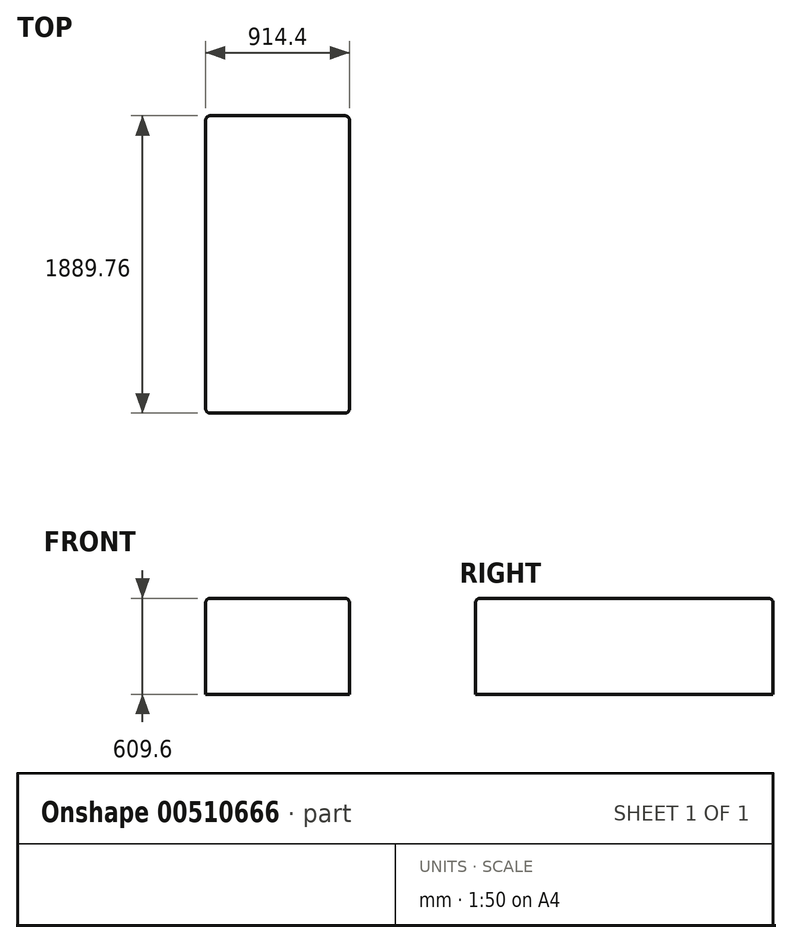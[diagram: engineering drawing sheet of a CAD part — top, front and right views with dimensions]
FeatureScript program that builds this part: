
annotation { "Feature Type Name" : "Feature", "Feature Type Description" : "" }
export const myFeature = defineFeature(function(context is Context, id is Id, definition is map)
    precondition{}
    {
        {
            var Q0;
            Q0=qCreatedBy(makeId("Top.planeOp"),FACE);
            var sketch = newSketch(context, id + "F0", { "sketchPlane" : qUnion([Q0])});
            skLineSegment(sketch, "E0.bottom", {"start": v(-470.27, 741.45) * mm, "end": v(444.13, 741.45) * mm});
            skLineSegment(sketch, "E0.top", {"start": v(-470.27, -1148.3) * mm, "end": v(444.13, -1148.3) * mm});
            skLineSegment(sketch, "E0.left", {"start": v(-470.27, 741.45) * mm, "end": v(-470.27, -1148.3) * mm});
            skLineSegment(sketch, "E0.right", {"start": v(444.13, 741.45) * mm, "end": v(444.13, -1148.3) * mm});
            skSolve(sketch);
        }
        {
            var Q0;
            Q0 = qSketchRegion(id + "F0", true);
            extrude(context, id + "F1", {"entities" : qUnion([Q0]), "depth" : 609.6 * mm, "offsetDistance" : 30.48 * mm});
        }
        {
            var Q0;
            Q0=makeQuery(id+"F1.opExtrude","CAP_EDGE",EDGE,{"disambiguationData":[OSD([sQuery(id+"F0.wireOp",EDGE,"E0.left")])],"isStart":false});
            var Q1;
            Q1=makeQuery(id+"F1.opExtrude","CAP_EDGE",EDGE,{"disambiguationData":[OSD([sQuery(id+"F0.wireOp",EDGE,"E0.bottom")])],"isStart":false});
            var Q2;
            Q2=makeQuery(id+"F1.opExtrude","CAP_EDGE",EDGE,{"disambiguationData":[OSD([sQuery(id+"F0.wireOp",EDGE,"E0.right")])],"isStart":false});
            var Q3;
            Q3=makeQuery(id+"F1.opExtrude","CAP_EDGE",EDGE,{"disambiguationData":[OSD([sQuery(id+"F0.wireOp",EDGE,"E0.top")])],"isStart":false});
            fillet(context, id + "F2", {"entities" : qUnion([Q0, Q1, Q2, Q3]), "radius" : 30.48 * mm, "tangentPropagation" : true, "allowEdgeOverflow" : false});
        }
        {
            var Q0;
            Q0=makeQuery(id+"F2.opFillet","BLEND_EDGE",EDGE,{"blendedFrom":[makeQuery(id+"F1.opExtrude","CAP_EDGE",EDGE,{"disambiguationData":[OSD([sQuery(id+"F0.wireOp",EDGE,"E0.bottom")])],"isStart":false}),makeQuery(id+"F1.opExtrude","CAP_EDGE",EDGE,{"disambiguationData":[OSD([sQuery(id+"F0.wireOp",EDGE,"E0.left")])],"isStart":false})],"blendedInto":[]});
            var Q1;
            Q1=makeQuery(id+"F2.opFillet","BLEND_EDGE",EDGE,{"blendedFrom":[makeQuery(id+"F1.opExtrude","CAP_EDGE",EDGE,{"disambiguationData":[OSD([sQuery(id+"F0.wireOp",EDGE,"E0.bottom")])],"isStart":false}),makeQuery(id+"F1.opExtrude","CAP_EDGE",EDGE,{"disambiguationData":[OSD([sQuery(id+"F0.wireOp",EDGE,"E0.right")])],"isStart":false})],"blendedInto":[]});
            var Q2;
            Q2=makeQuery(id+"F2.opFillet","BLEND_EDGE",EDGE,{"blendedFrom":[makeQuery(id+"F1.opExtrude","CAP_EDGE",EDGE,{"disambiguationData":[OSD([sQuery(id+"F0.wireOp",EDGE,"E0.top")])],"isStart":false}),makeQuery(id+"F1.opExtrude","CAP_EDGE",EDGE,{"disambiguationData":[OSD([sQuery(id+"F0.wireOp",EDGE,"E0.right")])],"isStart":false})],"blendedInto":[]});
            var Q3;
            Q3=makeQuery(id+"F2.opFillet","BLEND_EDGE",EDGE,{"blendedFrom":[makeQuery(id+"F1.opExtrude","CAP_EDGE",EDGE,{"disambiguationData":[OSD([sQuery(id+"F0.wireOp",EDGE,"E0.top")])],"isStart":false}),makeQuery(id+"F1.opExtrude","CAP_EDGE",EDGE,{"disambiguationData":[OSD([sQuery(id+"F0.wireOp",EDGE,"E0.left")])],"isStart":false})],"blendedInto":[]});
            fillet(context, id + "F3", {"entities" : qUnion([Q0, Q1, Q2, Q3]), "radius" : 30.48 * mm, "tangentPropagation" : true, "allowEdgeOverflow" : false});
        }
    });
